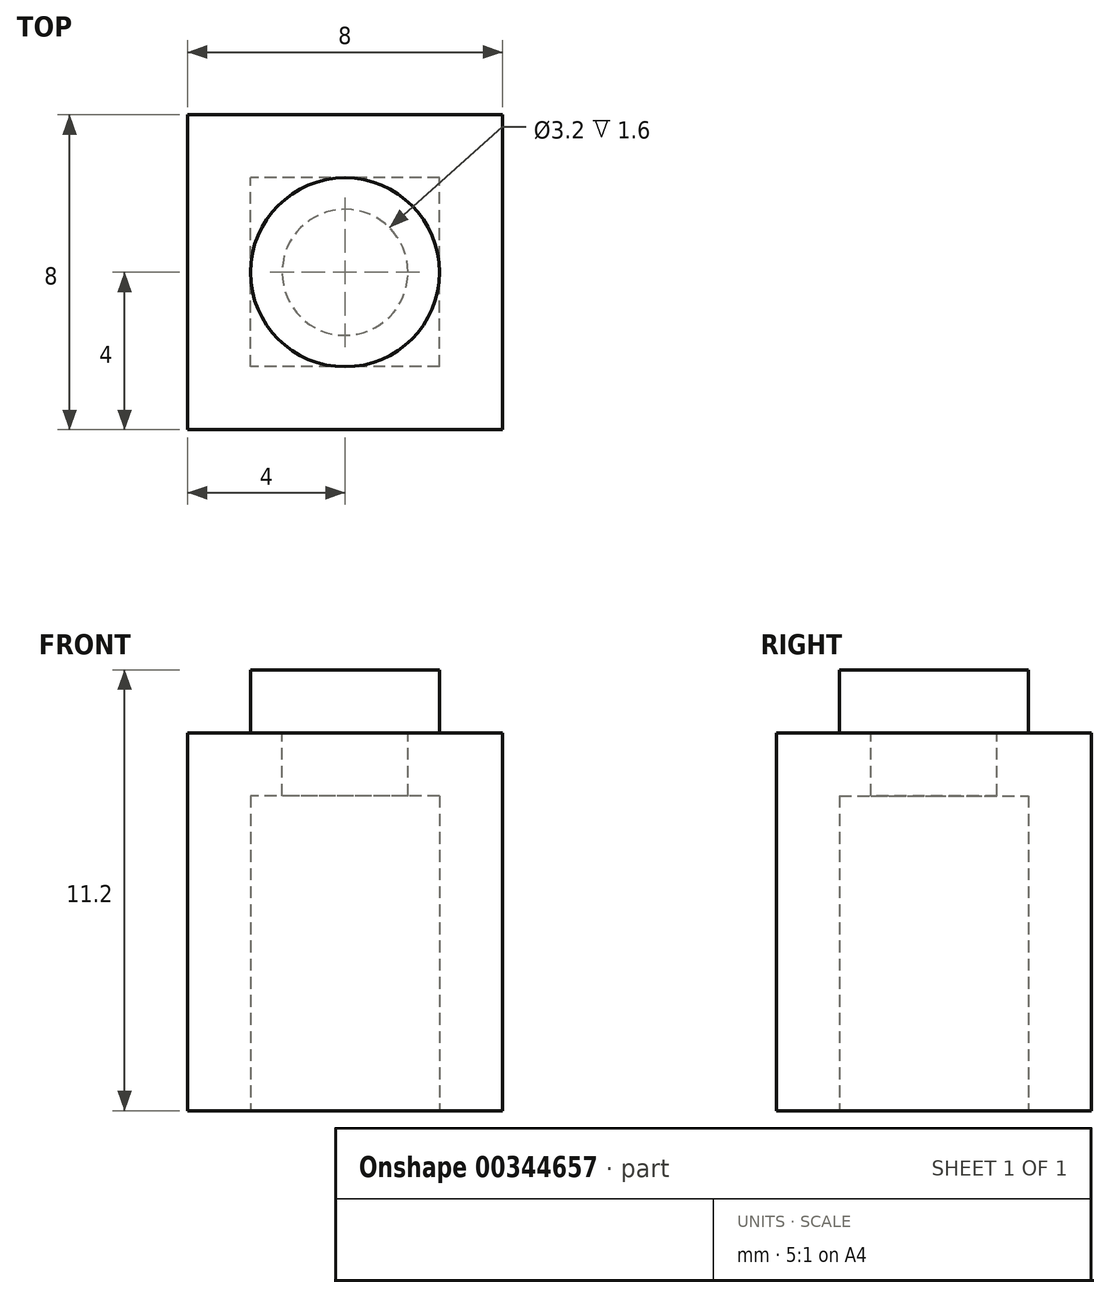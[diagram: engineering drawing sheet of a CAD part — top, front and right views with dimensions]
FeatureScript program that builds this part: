
annotation { "Feature Type Name" : "Feature", "Feature Type Description" : "" }
export const myFeature = defineFeature(function(context is Context, id is Id, definition is map)
    precondition{}
    {
        {
            var Q0;
            Q0=qCreatedBy(makeId("Top.planeOp"),FACE);
            var sketch = newSketch(context, id + "F0", { "sketchPlane" : qUnion([Q0])});
            skLineSegment(sketch, "E0.bottom", {"start": v(4, -4) * mm, "end": v(-4, -4) * mm});
            skLineSegment(sketch, "E0.top", {"start": v(4, 4) * mm, "end": v(-4, 4) * mm});
            skLineSegment(sketch, "E0.left", {"start": v(4, -4) * mm, "end": v(4, 4) * mm});
            skLineSegment(sketch, "E0.right", {"start": v(-4, -4) * mm, "end": v(-4, 4) * mm});
            skPoint(sketch, "E0.middle", {"position": v(0, 0) * mm});
            skLineSegment(sketch, "E1.0", {"start": v(2.4, -2.4) * mm, "end": v(-2.4, -2.4) * mm});
            skLineSegment(sketch, "E1.1", {"start": v(2.4, -2.4) * mm, "end": v(2.4, 2.4) * mm});
            skLineSegment(sketch, "E1.2", {"start": v(2.4, 2.4) * mm, "end": v(-2.4, 2.4) * mm});
            skLineSegment(sketch, "E1.3", {"start": v(-2.4, -2.4) * mm, "end": v(-2.4, 2.4) * mm});
            skSolve(sketch);
        }
        {
            var Q0;
            Q0 = qSketchRegion(id + "F0", true);
            var Q1;
            Q1=makeQuery(id+"F0.imprint","IMPRINT",FACE,{"disambiguationData":[TD([[makeQuery(id+"F0.imprint","IMPRINT",EDGE,{"derivedFrom":sQuery(id+"F0.wireOp",EDGE,"E1.0")}),-1.0]])]});
            extrude(context, id + "F1", {"entities" : qUnion([Q0, Q1]), "depth" : 9.6 * mm});
        }
        {
            var Q0;
            Q0=makeQuery(id+"F0.imprint","IMPRINT",FACE,{"disambiguationData":[TD([[makeQuery(id+"F0.imprint","IMPRINT",EDGE,{"derivedFrom":sQuery(id+"F0.wireOp",EDGE,"E1.0")}),-1.0]])]});
            extrude(context, id + "F2", {"entities" : qUnion([Q0]), "operationType" : NewBodyOperationType.REMOVE, "depth" : 8 * mm});
        }
        {
            var Q0;
            Q0=makeQuery(id+"F1.opExtrude","CAP_FACE",FACE,{"disambiguationData":[OSD([sQuery(id+"F0.wireOp",EDGE,"E0.bottom"),sQuery(id+"F0.wireOp",EDGE,"E0.top"),sQuery(id+"F0.wireOp",EDGE,"E0.left"),sQuery(id+"F0.wireOp",EDGE,"E0.right")])],"isStart":false});
            var sketch = newSketch(context, id + "F3", { "sketchPlane" : qUnion([Q0])});
            skCircle(sketch, "E2", {"center": v(0, 0) * mm, "radius": 1.6 * mm});
            skSolve(sketch);
        }
        {
            var Q0;
            Q0 = qSketchRegion(id + "F3", true);
            extrude(context, id + "F4", {"entities" : qUnion([Q0]), "operationType" : NewBodyOperationType.REMOVE, "oppositeDirection" : true, "depth" : 1.6 * mm});
        }
        {
            var Q0;
            Q0=makeQuery(id+"F1.opExtrude","CAP_FACE",FACE,{"disambiguationData":[OSD([sQuery(id+"F0.wireOp",EDGE,"E0.bottom"),sQuery(id+"F0.wireOp",EDGE,"E0.top"),sQuery(id+"F0.wireOp",EDGE,"E0.left"),sQuery(id+"F0.wireOp",EDGE,"E0.right")])],"isStart":false});
            var sketch = newSketch(context, id + "F5", { "sketchPlane" : qUnion([Q0])});
            skCircle(sketch, "E3", {"center": v(0, 0) * mm, "radius": 2.4 * mm});
            skSolve(sketch);
        }
        {
            var Q0;
            Q0 = qSketchRegion(id + "F5", true);
            extrude(context, id + "F6", {"entities" : qUnion([Q0]), "operationType" : NewBodyOperationType.ADD, "depth" : 1.6 * mm});
        }
    });
